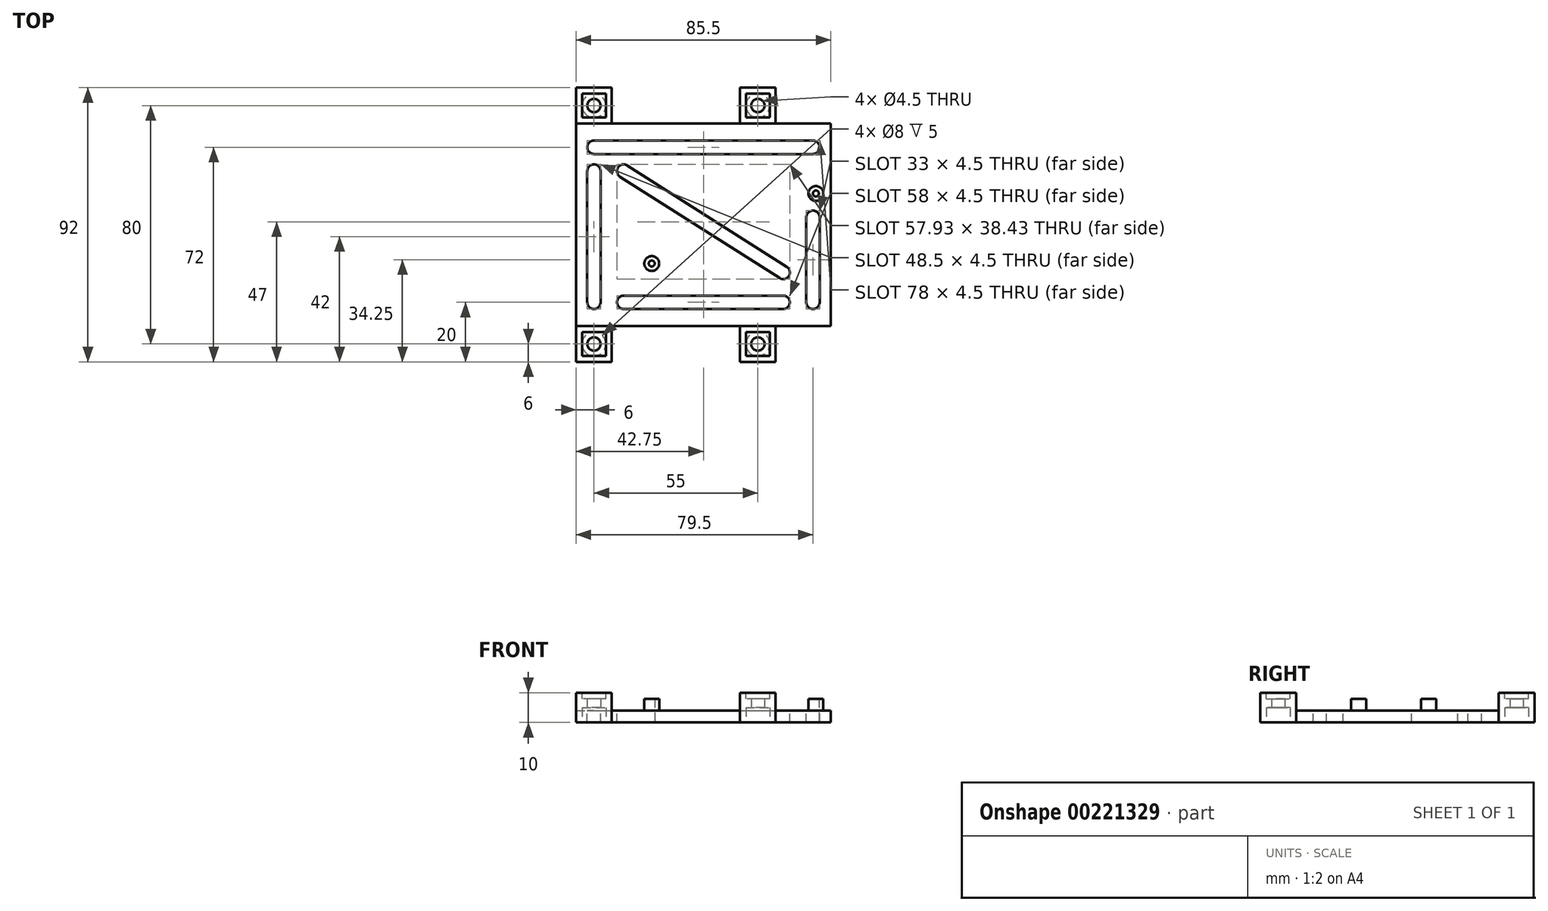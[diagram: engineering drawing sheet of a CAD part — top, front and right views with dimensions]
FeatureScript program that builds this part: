
annotation { "Feature Type Name" : "Feature", "Feature Type Description" : "" }
export const myFeature = defineFeature(function(context is Context, id is Id, definition is map)
    precondition{}
    {
        {
            var Q0;
            Q0=qCreatedBy(makeId("Top.planeOp"),FACE);
            var sketch = newSketch(context, id + "F0", { "sketchPlane" : qUnion([Q0])});
            skLineSegment(sketch, "E0", {"start": v(-55.4, 46) * mm, "end": v(-55.4, -46) * mm});
            skLineSegment(sketch, "E1", {"start": v(-55.4, -46) * mm, "end": v(-43.4, -46) * mm});
            skLineSegment(sketch, "E2", {"start": v(-43.4, -46) * mm, "end": v(-43.4, -34) * mm});
            skLineSegment(sketch, "E3", {"start": v(-43.4, -34) * mm, "end": v(-0.4, -34) * mm});
            skLineSegment(sketch, "E4", {"start": v(-0.4, -34) * mm, "end": v(-0.4, -46) * mm});
            skLineSegment(sketch, "E5", {"start": v(-0.4, -46) * mm, "end": v(11.6, -46) * mm});
            skLineSegment(sketch, "E6", {"start": v(11.6, -46) * mm, "end": v(11.6, -34) * mm});
            skLineSegment(sketch, "E7", {"start": v(11.6, -34) * mm, "end": v(30.1, -34) * mm});
            skLineSegment(sketch, "E8", {"start": v(30.1, -34) * mm, "end": v(30.1, 34) * mm});
            skLineSegment(sketch, "E9", {"start": v(30.1, 34) * mm, "end": v(11.6, 34) * mm});
            skLineSegment(sketch, "E10", {"start": v(11.6, 34) * mm, "end": v(11.6, 46) * mm});
            skLineSegment(sketch, "E11", {"start": v(11.6, 46) * mm, "end": v(-0.4, 46) * mm});
            skLineSegment(sketch, "E12", {"start": v(-0.4, 46) * mm, "end": v(-0.4, 34) * mm});
            skLineSegment(sketch, "E13", {"start": v(-0.4, 34) * mm, "end": v(-43.4, 34) * mm});
            skLineSegment(sketch, "E14", {"start": v(-43.4, 34) * mm, "end": v(-43.4, 46) * mm});
            skLineSegment(sketch, "E15", {"start": v(-43.4, 46) * mm, "end": v(-55.4, 46) * mm});
            skCircle(sketch, "E16", {"center": v(5.6, 40) * mm, "radius": 2.25 * mm});
            skPoint(sketch, "E16.centerSnap0", {"position": v(5.6, 46) * mm});
            skCircle(sketch, "E17", {"center": v(5.6, -40) * mm, "radius": 2.25 * mm});
            skPoint(sketch, "E17.centerSnap0", {"position": v(5.6, -46) * mm});
            skCircle(sketch, "E18", {"center": v(-49.4, -40) * mm, "radius": 2.25 * mm});
            skPoint(sketch, "E18.centerSnap0", {"position": v(-49.4, -46) * mm});
            skCircle(sketch, "E19", {"center": v(-49.4, 40) * mm, "radius": 2.25 * mm});
            skPoint(sketch, "E19.centerSnap0", {"position": v(-49.4, 46) * mm});
            skLineSegment(sketch, "E20", {"start": v(-49.4, -46) * mm, "end": v(-49.4, -40) * mm, "construction": true});
            skLineSegment(sketch, "E21", {"start": v(5.6, -46) * mm, "end": v(5.6, -40) * mm, "construction": true});
            skLineSegment(sketch, "E22", {"start": v(-49.4, 46) * mm, "end": v(-49.4, 40) * mm, "construction": true});
            skLineSegment(sketch, "E23", {"start": v(5.6, 46) * mm, "end": v(5.6, 40) * mm, "construction": true});
            skLineSegment(sketch, "E24", {"start": v(-43.4, 34) * mm, "end": v(0, 0) * mm, "construction": true});
            skLineSegment(sketch, "E25", {"start": v(0, 0) * mm, "end": v(-43.4, -34) * mm, "construction": true});
            skLineSegment(sketch, "E26.bottom", {"start": v(-30, 10.5) * mm, "end": v(25.1, 10.5) * mm, "construction": true});
            skLineSegment(sketch, "E26.top", {"start": v(-30, -13) * mm, "end": v(25.1, -13) * mm, "construction": true});
            skLineSegment(sketch, "E26.left", {"start": v(-30, 10.5) * mm, "end": v(-30, -13) * mm, "construction": true});
            skLineSegment(sketch, "E26.right", {"start": v(25.1, 10.5) * mm, "end": v(25.1, -13) * mm, "construction": true});
            skCircle(sketch, "E27", {"center": v(25.1, 10.5) * mm, "radius": 1 * mm});
            skCircle(sketch, "E28", {"center": v(-30, -13) * mm, "radius": 1 * mm});
            skSolve(sketch);
        }
        {
            var Q0;
            Q0=makeQuery(id+"F0.imprint","IMPRINT",FACE,{"disambiguationData":[TD([[makeQuery(id+"F0.imprint","IMPRINT",EDGE,{"derivedFrom":sQuery(id+"F0.wireOp",EDGE,"E0")}),1.0]])]});
            extrude(context, id + "F1", {"entities" : qUnion([Q0]), "depth" : 4 * mm});
        }
        {
            var Q0;
            Q0=makeQuery(id+"F1.opExtrude","CAP_FACE",FACE,{"disambiguationData":[OSD([sQuery(id+"F0.wireOp",EDGE,"E0"),sQuery(id+"F0.wireOp",EDGE,"E1"),sQuery(id+"F0.wireOp",EDGE,"E2"),sQuery(id+"F0.wireOp",EDGE,"E3"),sQuery(id+"F0.wireOp",EDGE,"E4"),sQuery(id+"F0.wireOp",EDGE,"E5"),sQuery(id+"F0.wireOp",EDGE,"E6"),sQuery(id+"F0.wireOp",EDGE,"E7"),sQuery(id+"F0.wireOp",EDGE,"E8"),sQuery(id+"F0.wireOp",EDGE,"E9"),sQuery(id+"F0.wireOp",EDGE,"E10"),sQuery(id+"F0.wireOp",EDGE,"E11"),sQuery(id+"F0.wireOp",EDGE,"E12"),sQuery(id+"F0.wireOp",EDGE,"E13"),sQuery(id+"F0.wireOp",EDGE,"E14"),sQuery(id+"F0.wireOp",EDGE,"E15"),sQuery(id+"F0.wireOp",EDGE,"E16"),sQuery(id+"F0.wireOp",EDGE,"E17"),sQuery(id+"F0.wireOp",EDGE,"E18"),sQuery(id+"F0.wireOp",EDGE,"E19"),sQuery(id+"F0.wireOp",EDGE,"OmNVu6tG-rWnz-weHn-Idnk-AImVxQJASrev"),sQuery(id+"F0.wireOp",EDGE,"E27"),sQuery(id+"F0.wireOp",EDGE,"SQ5UMAVa-DhAk-clRl-90om-H450dHhwvuaT"),sQuery(id+"F0.wireOp",EDGE,"E28")])],"isStart":false});
            var sketch = newSketch(context, id + "F2", { "sketchPlane" : qUnion([Q0])});
            skLineSegment(sketch, "E29.bottom", {"start": v(-55.4, -46) * mm, "end": v(-43.4, -46) * mm});
            skLineSegment(sketch, "E29.top", {"start": v(-55.4, -34) * mm, "end": v(-43.4, -34) * mm});
            skLineSegment(sketch, "E29.left", {"start": v(-55.4, -46) * mm, "end": v(-55.4, -34) * mm});
            skLineSegment(sketch, "E29.right", {"start": v(-43.4, -46) * mm, "end": v(-43.4, -34) * mm});
            skLineSegment(sketch, "E30.bottom", {"start": v(-55.4, 46) * mm, "end": v(-43.4, 46) * mm});
            skLineSegment(sketch, "E30.top", {"start": v(-55.4, 34) * mm, "end": v(-43.4, 34) * mm});
            skLineSegment(sketch, "E30.left", {"start": v(-55.4, 46) * mm, "end": v(-55.4, 34) * mm});
            skLineSegment(sketch, "E30.right", {"start": v(-43.4, 46) * mm, "end": v(-43.4, 34) * mm});
            skLineSegment(sketch, "E31.bottom", {"start": v(-0.4, 46) * mm, "end": v(11.6, 46) * mm});
            skLineSegment(sketch, "E31.top", {"start": v(-0.4, 34) * mm, "end": v(11.6, 34) * mm});
            skLineSegment(sketch, "E31.left", {"start": v(-0.4, 46) * mm, "end": v(-0.4, 34) * mm});
            skLineSegment(sketch, "E31.right", {"start": v(11.6, 46) * mm, "end": v(11.6, 34) * mm});
            skLineSegment(sketch, "E32.bottom", {"start": v(-0.4, -34) * mm, "end": v(11.6, -34) * mm});
            skLineSegment(sketch, "E32.top", {"start": v(-0.4, -46) * mm, "end": v(11.6, -46) * mm});
            skLineSegment(sketch, "E32.left", {"start": v(-0.4, -34) * mm, "end": v(-0.4, -46) * mm});
            skLineSegment(sketch, "E32.right", {"start": v(11.6, -34) * mm, "end": v(11.6, -46) * mm});
            skSolve(sketch);
        }
        {
            var Q0;
            Q0=makeQuery(id+"F2.imprint","IMPRINT",FACE,{"disambiguationData":[TD([[makeQuery(id+"F2.imprint","IMPRINT",EDGE,{"derivedFrom":sQuery(id+"F2.wireOp",EDGE,"E29.bottom")}),1.0]])]});
            var Q1;
            Q1=makeQuery(id+"F2.imprint","IMPRINT",FACE,{"disambiguationData":[TD([[makeQuery(id+"F2.imprint","IMPRINT",EDGE,{"derivedFrom":sQuery(id+"F2.wireOp",EDGE,"E30.bottom")}),1.0]])]});
            var Q2;
            Q2=makeQuery(id+"F2.imprint","IMPRINT",FACE,{"disambiguationData":[TD([[makeQuery(id+"F2.imprint","IMPRINT",EDGE,{"derivedFrom":sQuery(id+"F2.wireOp",EDGE,"E31.bottom")}),1.0]])]});
            var Q3;
            Q3=makeQuery(id+"F2.imprint","IMPRINT",FACE,{"disambiguationData":[TD([[makeQuery(id+"F2.imprint","IMPRINT",EDGE,{"derivedFrom":sQuery(id+"F2.wireOp",EDGE,"E32.bottom")}),-1.0]])]});
            extrude(context, id + "F3", {"entities" : qUnion([Q0, Q1, Q2, Q3]), "operationType" : NewBodyOperationType.ADD, "depth" : 6 * mm});
        }
        {
            var Q0;
            Q0=makeQuery(id+"F3.opExtrude","CAP_FACE",FACE,{"disambiguationData":[OSD([sQuery(id+"F0.wireOp",EDGE,"E18"),sQuery(id+"F2.wireOp",EDGE,"E29.bottom"),sQuery(id+"F2.wireOp",EDGE,"E29.top"),sQuery(id+"F2.wireOp",EDGE,"E29.left"),sQuery(id+"F2.wireOp",EDGE,"E29.right")])],"isStart":false});
            var sketch = newSketch(context, id + "F4", { "sketchPlane" : qUnion([Q0])});
            skCircle(sketch, "E33.0", {"center": v(-49.4, 40) * mm, "radius": 2.25 * mm, "construction": true});
            skCircle(sketch, "E33.1", {"center": v(5.6, 40) * mm, "radius": 2.25 * mm, "construction": true});
            skCircle(sketch, "E33.2", {"center": v(5.6, -40) * mm, "radius": 2.25 * mm, "construction": true});
            skCircle(sketch, "E33.3", {"center": v(-49.4, -40) * mm, "radius": 2.25 * mm, "construction": true});
            skLineSegment(sketch, "E34.bottom", {"start": v(-45.4, 44) * mm, "end": v(-53.4, 44) * mm});
            skLineSegment(sketch, "E34.top", {"start": v(-45.4, 36) * mm, "end": v(-53.4, 36) * mm});
            skLineSegment(sketch, "E34.left", {"start": v(-45.4, 44) * mm, "end": v(-45.4, 36) * mm});
            skLineSegment(sketch, "E34.right", {"start": v(-53.4, 44) * mm, "end": v(-53.4, 36) * mm});
            skLineSegment(sketch, "E35.bottom", {"start": v(9.6, 44) * mm, "end": v(1.6, 44) * mm});
            skLineSegment(sketch, "E35.top", {"start": v(9.6, 36) * mm, "end": v(1.6, 36) * mm});
            skLineSegment(sketch, "E35.left", {"start": v(9.6, 44) * mm, "end": v(9.6, 36) * mm});
            skLineSegment(sketch, "E35.right", {"start": v(1.6, 44) * mm, "end": v(1.6, 36) * mm});
            skLineSegment(sketch, "E36.bottom", {"start": v(9.6, -44) * mm, "end": v(1.6, -44) * mm});
            skLineSegment(sketch, "E36.top", {"start": v(9.6, -36) * mm, "end": v(1.6, -36) * mm});
            skLineSegment(sketch, "E36.left", {"start": v(9.6, -44) * mm, "end": v(9.6, -36) * mm});
            skLineSegment(sketch, "E36.right", {"start": v(1.6, -44) * mm, "end": v(1.6, -36) * mm});
            skLineSegment(sketch, "E37.bottom", {"start": v(-53.4, -44) * mm, "end": v(-45.4, -44) * mm});
            skLineSegment(sketch, "E37.top", {"start": v(-53.4, -36) * mm, "end": v(-45.4, -36) * mm});
            skLineSegment(sketch, "E37.left", {"start": v(-53.4, -44) * mm, "end": v(-53.4, -36) * mm});
            skLineSegment(sketch, "E37.right", {"start": v(-45.4, -44) * mm, "end": v(-45.4, -36) * mm});
            skSolve(sketch);
        }
        {
            var Q0;
            Q0=makeQuery(id+"F4.imprint","IMPRINT",FACE,{"disambiguationData":[TD([[makeQuery(id+"F4.imprint","IMPRINT",EDGE,{"derivedFrom":sQuery(id+"F4.wireOp",EDGE,"E34.bottom")}),1.0]])]});
            var Q1;
            Q1=makeQuery(id+"F4.imprint","IMPRINT",FACE,{"disambiguationData":[TD([[makeQuery(id+"F4.imprint","IMPRINT",EDGE,{"derivedFrom":sQuery(id+"F4.wireOp",EDGE,"E35.bottom")}),1.0]])]});
            var Q2;
            Q2=makeQuery(id+"F4.imprint","IMPRINT",FACE,{"disambiguationData":[TD([[makeQuery(id+"F4.imprint","IMPRINT",EDGE,{"derivedFrom":sQuery(id+"F4.wireOp",EDGE,"E36.bottom")}),-1.0]])]});
            var Q3;
            Q3=makeQuery(id+"F4.imprint","IMPRINT",FACE,{"disambiguationData":[TD([[makeQuery(id+"F4.imprint","IMPRINT",EDGE,{"derivedFrom":sQuery(id+"F4.wireOp",EDGE,"E37.bottom")}),1.0]])]});
            extrude(context, id + "F5", {"entities" : qUnion([Q0, Q1, Q2, Q3]), "operationType" : NewBodyOperationType.REMOVE, "oppositeDirection" : true, "depth" : 2 * mm});
        }
        {
            var Q0;
            Q0=makeQuery(id+"F1.opExtrude","CAP_FACE",FACE,{"disambiguationData":[OSD([sQuery(id+"F0.wireOp",EDGE,"E0"),sQuery(id+"F0.wireOp",EDGE,"E1"),sQuery(id+"F0.wireOp",EDGE,"E2"),sQuery(id+"F0.wireOp",EDGE,"E3"),sQuery(id+"F0.wireOp",EDGE,"E4"),sQuery(id+"F0.wireOp",EDGE,"E5"),sQuery(id+"F0.wireOp",EDGE,"E6"),sQuery(id+"F0.wireOp",EDGE,"E7"),sQuery(id+"F0.wireOp",EDGE,"E8"),sQuery(id+"F0.wireOp",EDGE,"E9"),sQuery(id+"F0.wireOp",EDGE,"E10"),sQuery(id+"F0.wireOp",EDGE,"E11"),sQuery(id+"F0.wireOp",EDGE,"E12"),sQuery(id+"F0.wireOp",EDGE,"E13"),sQuery(id+"F0.wireOp",EDGE,"E14"),sQuery(id+"F0.wireOp",EDGE,"E15"),sQuery(id+"F0.wireOp",EDGE,"E16"),sQuery(id+"F0.wireOp",EDGE,"E17"),sQuery(id+"F0.wireOp",EDGE,"E18"),sQuery(id+"F0.wireOp",EDGE,"E19"),sQuery(id+"F0.wireOp",EDGE,"OmNVu6tG-rWnz-weHn-Idnk-AImVxQJASrev"),sQuery(id+"F0.wireOp",EDGE,"E27"),sQuery(id+"F0.wireOp",EDGE,"SQ5UMAVa-DhAk-clRl-90om-H450dHhwvuaT"),sQuery(id+"F0.wireOp",EDGE,"E28")])],"isStart":true});
            var sketch = newSketch(context, id + "F6", { "sketchPlane" : qUnion([Q0])});
            skCircle(sketch, "E38", {"center": v(-49.4, 40) * mm, "radius": 4 * mm});
            skCircle(sketch, "E39", {"center": v(5.6, 40) * mm, "radius": 4 * mm});
            skCircle(sketch, "E40", {"center": v(5.6, -40) * mm, "radius": 4 * mm});
            skCircle(sketch, "E41", {"center": v(-49.4, -40) * mm, "radius": 4 * mm});
            skSolve(sketch);
        }
        {
            var Q0;
            Q0=makeQuery(id+"F6.imprint","IMPRINT",FACE,{"disambiguationData":[TD([[makeQuery(id+"F6.imprint","IMPRINT",EDGE,{"derivedFrom":sQuery(id+"F6.wireOp",EDGE,"E38")}),1.0]])]});
            var Q1;
            Q1=makeQuery(id+"F6.imprint","IMPRINT",FACE,{"disambiguationData":[TD([[makeQuery(id+"F6.imprint","IMPRINT",EDGE,{"derivedFrom":sQuery(id+"F6.wireOp",EDGE,"E39")}),1.0]])]});
            var Q2;
            Q2=makeQuery(id+"F6.imprint","IMPRINT",FACE,{"disambiguationData":[TD([[makeQuery(id+"F6.imprint","IMPRINT",EDGE,{"derivedFrom":sQuery(id+"F6.wireOp",EDGE,"E40")}),1.0]])]});
            var Q3;
            Q3=makeQuery(id+"F6.imprint","IMPRINT",FACE,{"disambiguationData":[TD([[makeQuery(id+"F6.imprint","IMPRINT",EDGE,{"derivedFrom":sQuery(id+"F6.wireOp",EDGE,"E41")}),1.0]])]});
            extrude(context, id + "F7", {"entities" : qUnion([Q0, Q1, Q2, Q3]), "operationType" : NewBodyOperationType.REMOVE, "oppositeDirection" : true, "depth" : 5 * mm});
        }
        {
            var Q0;
            Q0=makeQuery(id+"F1.opExtrude","CAP_FACE",FACE,{"disambiguationData":[OSD([sQuery(id+"F0.wireOp",EDGE,"E0"),sQuery(id+"F0.wireOp",EDGE,"E1"),sQuery(id+"F0.wireOp",EDGE,"E2"),sQuery(id+"F0.wireOp",EDGE,"E3"),sQuery(id+"F0.wireOp",EDGE,"E4"),sQuery(id+"F0.wireOp",EDGE,"E5"),sQuery(id+"F0.wireOp",EDGE,"E6"),sQuery(id+"F0.wireOp",EDGE,"E7"),sQuery(id+"F0.wireOp",EDGE,"E8"),sQuery(id+"F0.wireOp",EDGE,"E9"),sQuery(id+"F0.wireOp",EDGE,"E10"),sQuery(id+"F0.wireOp",EDGE,"E11"),sQuery(id+"F0.wireOp",EDGE,"E12"),sQuery(id+"F0.wireOp",EDGE,"E13"),sQuery(id+"F0.wireOp",EDGE,"E14"),sQuery(id+"F0.wireOp",EDGE,"E15"),sQuery(id+"F0.wireOp",EDGE,"E16"),sQuery(id+"F0.wireOp",EDGE,"E17"),sQuery(id+"F0.wireOp",EDGE,"E18"),sQuery(id+"F0.wireOp",EDGE,"E19"),sQuery(id+"F0.wireOp",EDGE,"OmNVu6tG-rWnz-weHn-Idnk-AImVxQJASrev"),sQuery(id+"F0.wireOp",EDGE,"E27"),sQuery(id+"F0.wireOp",EDGE,"SQ5UMAVa-DhAk-clRl-90om-H450dHhwvuaT"),sQuery(id+"F0.wireOp",EDGE,"E28")])],"isStart":false});
            var sketch = newSketch(context, id + "F8", { "sketchPlane" : qUnion([Q0])});
            skCircle(sketch, "E42", {"center": v(-30, -13) * mm, "radius": 2.5 * mm});
            skCircle(sketch, "E43", {"center": v(25.1, 10.5) * mm, "radius": 2.5 * mm});
            skSolve(sketch);
        }
        {
            var Q0;
            Q0=makeQuery(id+"F8.imprint","IMPRINT",FACE,{"disambiguationData":[TD([[makeQuery(id+"F8.imprint","IMPRINT",EDGE,{"derivedFrom":sQuery(id+"F8.wireOp",EDGE,"gE3oUv3f-fnfz-4OHR-KM7l-jvzw38WIQ6fo")}),1.0]])]});
            var Q1;
            Q1=makeQuery(id+"F8.imprint","IMPRINT",FACE,{"disambiguationData":[TD([[makeQuery(id+"F8.imprint","IMPRINT",EDGE,{"derivedFrom":sQuery(id+"F8.wireOp",EDGE,"E42")}),1.0]])]});
            var Q2;
            Q2=makeQuery(id+"F8.imprint","IMPRINT",FACE,{"disambiguationData":[TD([[makeQuery(id+"F8.imprint","IMPRINT",EDGE,{"derivedFrom":sQuery(id+"F8.wireOp",EDGE,"UACYHYFA-RfOP-6ulv-uorA-5RQTcs1Hd0xE")}),1.0]])]});
            var Q3;
            Q3=makeQuery(id+"F8.imprint","IMPRINT",FACE,{"disambiguationData":[TD([[makeQuery(id+"F8.imprint","IMPRINT",EDGE,{"derivedFrom":sQuery(id+"F8.wireOp",EDGE,"E43")}),1.0]])]});
            extrude(context, id + "F9", {"entities" : qUnion([Q0, Q1, Q2, Q3]), "operationType" : NewBodyOperationType.ADD, "depth" : 4 * mm});
        }
        {
            var Q0;
            Q0=makeQuery(id+"F1.opExtrude","CAP_FACE",FACE,{"disambiguationData":[OSD([sQuery(id+"F0.wireOp",EDGE,"E0"),sQuery(id+"F0.wireOp",EDGE,"E1"),sQuery(id+"F0.wireOp",EDGE,"E2"),sQuery(id+"F0.wireOp",EDGE,"E3"),sQuery(id+"F0.wireOp",EDGE,"E4"),sQuery(id+"F0.wireOp",EDGE,"E5"),sQuery(id+"F0.wireOp",EDGE,"E6"),sQuery(id+"F0.wireOp",EDGE,"E7"),sQuery(id+"F0.wireOp",EDGE,"E8"),sQuery(id+"F0.wireOp",EDGE,"E9"),sQuery(id+"F0.wireOp",EDGE,"E10"),sQuery(id+"F0.wireOp",EDGE,"E11"),sQuery(id+"F0.wireOp",EDGE,"E12"),sQuery(id+"F0.wireOp",EDGE,"E13"),sQuery(id+"F0.wireOp",EDGE,"E14"),sQuery(id+"F0.wireOp",EDGE,"E15"),sQuery(id+"F0.wireOp",EDGE,"E16"),sQuery(id+"F0.wireOp",EDGE,"E17"),sQuery(id+"F0.wireOp",EDGE,"E18"),sQuery(id+"F0.wireOp",EDGE,"E19"),sQuery(id+"F0.wireOp",EDGE,"OmNVu6tG-rWnz-weHn-Idnk-AImVxQJASrev"),sQuery(id+"F0.wireOp",EDGE,"E27"),sQuery(id+"F0.wireOp",EDGE,"SQ5UMAVa-DhAk-clRl-90om-H450dHhwvuaT"),sQuery(id+"F0.wireOp",EDGE,"E28")])],"isStart":false});
            var sketch = newSketch(context, id + "F10", { "sketchPlane" : qUnion([Q0])});
            skCircle(sketch, "E44", {"center": v(-49.4, 26) * mm, "radius": 2.25 * mm});
            skCircle(sketch, "E45", {"center": v(24.1, 26) * mm, "radius": 2.25 * mm});
            skCircle(sketch, "E46", {"center": v(-49.4, 18) * mm, "radius": 2.25 * mm});
            skCircle(sketch, "E47", {"center": v(-49.4, -26) * mm, "radius": 2.25 * mm});
            skCircle(sketch, "E48", {"center": v(24.1, -26) * mm, "radius": 2.25 * mm});
            skCircle(sketch, "E49", {"center": v(-39.4, -26) * mm, "radius": 2.25 * mm});
            skCircle(sketch, "E50", {"center": v(14.1, -26) * mm, "radius": 2.25 * mm});
            skLineSegment(sketch, "E51", {"start": v(-49.4, 28.25) * mm, "end": v(24.1, 28.25) * mm});
            skLineSegment(sketch, "E52", {"start": v(-49.4, 23.75) * mm, "end": v(24.1, 23.75) * mm});
            skLineSegment(sketch, "E53", {"start": v(-47.15, -26) * mm, "end": v(-47.15, 18) * mm});
            skLineSegment(sketch, "E54", {"start": v(14.1, -28.25) * mm, "end": v(-39.4, -28.25) * mm});
            skLineSegment(sketch, "E55", {"start": v(-39.4, -23.75) * mm, "end": v(14.1, -23.75) * mm});
            skLineSegment(sketch, "E56", {"start": v(-49.4, -26) * mm, "end": v(24.1, -26) * mm, "construction": true});
            skPoint(sketch, "E57", {"position": v(25.1, 10.5) * mm});
            skCircle(sketch, "E58", {"center": v(24.1, 2.5) * mm, "radius": 2.25 * mm});
            skLineSegment(sketch, "E59", {"start": v(21.85, 2.5) * mm, "end": v(21.85, -26) * mm});
            skLineSegment(sketch, "E60", {"start": v(26.35, 2.5) * mm, "end": v(26.35, -26) * mm});
            skLineSegment(sketch, "E61", {"start": v(-51.65, 18) * mm, "end": v(-51.65, -26) * mm});
            skLineSegment(sketch, "E62", {"start": v(-49.4, 26) * mm, "end": v(-49.4, 18) * mm, "construction": true});
            skLineSegment(sketch, "E63", {"start": v(24.1, 26) * mm, "end": v(24.1, 2.5) * mm, "construction": true});
            skCircle(sketch, "E64", {"center": v(-39.4, 18) * mm, "radius": 2.25 * mm});
            skCircle(sketch, "E65", {"center": v(14.1, -16) * mm, "radius": 2.25 * mm});
            skLineSegment(sketch, "E66", {"start": v(-38.2, 19.9) * mm, "end": v(15.3, -14.1) * mm});
            skLineSegment(sketch, "E67", {"start": v(12.9, -17.9) * mm, "end": v(-40.6, 16.1) * mm});
            skLineSegment(sketch, "E68", {"start": v(-49.4, 18) * mm, "end": v(-39.4, 18) * mm, "construction": true});
            skLineSegment(sketch, "E69", {"start": v(-39.4, -26) * mm, "end": v(-39.4, 18) * mm, "construction": true});
            skLineSegment(sketch, "E70", {"start": v(14.1, -26) * mm, "end": v(14.1, -16) * mm, "construction": true});
            skSolve(sketch);
        }
        {
            var Q0;
            {var subQ0=sQuery(id+"F10.wireOp",EDGE,"E51");Q0=makeQuery(id+"F10.imprint","IMPRINT",FACE,{"disambiguationData":[TD([[makeQuery(id+"F10.imprint","IMPRINT",EDGE,{"derivedFrom":subQ0}),-1.0]])]});}
            var Q1;
            {var subQ0=sQuery(id+"F10.wireOp",EDGE,"E44");var subQ1=makeQuery(id+"F10.imprint","INTERSECT",VERTEX,{"derivedFrom":[subQ0,sQuery(id+"F10.wireOp",EDGE,"E51")]});Q1=makeQuery(id+"F10.imprint","IMPRINT",FACE,{"disambiguationData":[TD([[makeQuery(id+"F10.imprint","IMPRINT",EDGE,{"disambiguationData":[TD([[subQ1,-1.0]])],"derivedFrom":subQ0}),1.0]])]});}
            var Q2;
            {var subQ0=sQuery(id+"F10.wireOp",EDGE,"E53");Q2=makeQuery(id+"F10.imprint","IMPRINT",FACE,{"disambiguationData":[TD([[makeQuery(id+"F10.imprint","IMPRINT",EDGE,{"derivedFrom":subQ0}),1.0]])]});}
            var Q3;
            {var subQ0=sQuery(id+"F10.wireOp",EDGE,"E46");var subQ1=makeQuery(id+"F10.imprint","INTERSECT",VERTEX,{"derivedFrom":[subQ0,sQuery(id+"F10.wireOp",EDGE,"E53")]});Q3=makeQuery(id+"F10.imprint","IMPRINT",FACE,{"disambiguationData":[TD([[makeQuery(id+"F10.imprint","IMPRINT",EDGE,{"disambiguationData":[TD([[subQ1,-1.0]])],"derivedFrom":subQ0}),1.0]])]});}
            var Q4;
            {var subQ0=sQuery(id+"F10.wireOp",EDGE,"E64");var subQ1=makeQuery(id+"F10.imprint","INTERSECT",VERTEX,{"derivedFrom":[subQ0,sQuery(id+"F10.wireOp",EDGE,"E66")]});Q4=makeQuery(id+"F10.imprint","IMPRINT",FACE,{"disambiguationData":[TD([[makeQuery(id+"F10.imprint","IMPRINT",EDGE,{"disambiguationData":[TD([[subQ1,-1.0]])],"derivedFrom":subQ0}),1.0]])]});}
            var Q5;
            {var subQ0=sQuery(id+"F10.wireOp",EDGE,"E47");var subQ1=makeQuery(id+"F10.imprint","INTERSECT",VERTEX,{"derivedFrom":[subQ0,sQuery(id+"F10.wireOp",EDGE,"E53")]});Q5=makeQuery(id+"F10.imprint","IMPRINT",FACE,{"disambiguationData":[TD([[makeQuery(id+"F10.imprint","IMPRINT",EDGE,{"disambiguationData":[TD([[subQ1,-1.0]])],"derivedFrom":subQ0}),1.0]])]});}
            var Q6;
            {var subQ0=sQuery(id+"F10.wireOp",EDGE,"E49");var subQ1=makeQuery(id+"F10.imprint","INTERSECT",VERTEX,{"derivedFrom":[subQ0,sQuery(id+"F10.wireOp",EDGE,"E54")]});Q6=makeQuery(id+"F10.imprint","IMPRINT",FACE,{"disambiguationData":[TD([[makeQuery(id+"F10.imprint","IMPRINT",EDGE,{"disambiguationData":[TD([[subQ1,1.0]])],"derivedFrom":subQ0}),1.0]])]});}
            var Q7;
            {var subQ0=sQuery(id+"F10.wireOp",EDGE,"E54");Q7=makeQuery(id+"F10.imprint","IMPRINT",FACE,{"disambiguationData":[TD([[makeQuery(id+"F10.imprint","IMPRINT",EDGE,{"derivedFrom":subQ0}),-1.0]])]});}
            var Q8;
            {var subQ0=sQuery(id+"F10.wireOp",EDGE,"E50");var subQ1=makeQuery(id+"F10.imprint","INTERSECT",VERTEX,{"derivedFrom":[subQ0,sQuery(id+"F10.wireOp",EDGE,"E54")]});Q8=makeQuery(id+"F10.imprint","IMPRINT",FACE,{"disambiguationData":[TD([[makeQuery(id+"F10.imprint","IMPRINT",EDGE,{"disambiguationData":[TD([[subQ1,1.0]])],"derivedFrom":subQ0}),1.0]])]});}
            var Q9;
            {var subQ0=sQuery(id+"F10.wireOp",EDGE,"E48");var subQ1=makeQuery(id+"F10.imprint","INTERSECT",VERTEX,{"derivedFrom":[subQ0,sQuery(id+"F10.wireOp",EDGE,"E59")]});Q9=makeQuery(id+"F10.imprint","IMPRINT",FACE,{"disambiguationData":[TD([[makeQuery(id+"F10.imprint","IMPRINT",EDGE,{"disambiguationData":[TD([[subQ1,1.0]])],"derivedFrom":subQ0}),1.0]])]});}
            var Q10;
            {var subQ0=sQuery(id+"F10.wireOp",EDGE,"E65");var subQ1=makeQuery(id+"F10.imprint","INTERSECT",VERTEX,{"derivedFrom":[subQ0,sQuery(id+"F10.wireOp",EDGE,"E66")]});Q10=makeQuery(id+"F10.imprint","IMPRINT",FACE,{"disambiguationData":[TD([[makeQuery(id+"F10.imprint","IMPRINT",EDGE,{"disambiguationData":[TD([[subQ1,-1.0]])],"derivedFrom":subQ0}),1.0]])]});}
            var Q11;
            {var subQ0=sQuery(id+"F10.wireOp",EDGE,"E66");Q11=makeQuery(id+"F10.imprint","IMPRINT",FACE,{"disambiguationData":[TD([[makeQuery(id+"F10.imprint","IMPRINT",EDGE,{"derivedFrom":subQ0}),-1.0]])]});}
            var Q12;
            {var subQ0=sQuery(id+"F10.wireOp",EDGE,"E59");Q12=makeQuery(id+"F10.imprint","IMPRINT",FACE,{"disambiguationData":[TD([[makeQuery(id+"F10.imprint","IMPRINT",EDGE,{"derivedFrom":subQ0}),1.0]])]});}
            var Q13;
            {var subQ0=sQuery(id+"F10.wireOp",EDGE,"E58");var subQ1=makeQuery(id+"F10.imprint","INTERSECT",VERTEX,{"derivedFrom":[subQ0,sQuery(id+"F10.wireOp",EDGE,"E59")]});Q13=makeQuery(id+"F10.imprint","IMPRINT",FACE,{"disambiguationData":[TD([[makeQuery(id+"F10.imprint","IMPRINT",EDGE,{"disambiguationData":[TD([[subQ1,1.0]])],"derivedFrom":subQ0}),1.0]])]});}
            var Q14;
            {var subQ0=sQuery(id+"F10.wireOp",EDGE,"E45");var subQ1=makeQuery(id+"F10.imprint","INTERSECT",VERTEX,{"derivedFrom":[subQ0,sQuery(id+"F10.wireOp",EDGE,"E51")]});Q14=makeQuery(id+"F10.imprint","IMPRINT",FACE,{"disambiguationData":[TD([[makeQuery(id+"F10.imprint","IMPRINT",EDGE,{"disambiguationData":[TD([[subQ1,-1.0]])],"derivedFrom":subQ0}),1.0]])]});}
            extrude(context, id + "F11", {"entities" : qUnion([Q0, Q1, Q2, Q3, Q4, Q5, Q6, Q7, Q8, Q9, Q10, Q11, Q12, Q13, Q14]), "operationType" : NewBodyOperationType.REMOVE, "endBound" : BoundingType.THROUGH_ALL, "oppositeDirection" : true, "depth" : 25 * mm});
        }
    });
